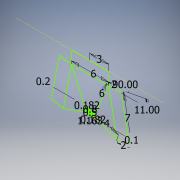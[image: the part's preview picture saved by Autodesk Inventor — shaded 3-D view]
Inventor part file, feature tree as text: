
AUTODESK INVENTOR PART (.ipt)
format: ipt  version: 2019.4 (Build 234330000, 330)  size: 112,128 bytes
history: native  units: in
note: dims shown in document units (in); Inventor stores cm internally (conversion verified against a paired STEP export)
features: sketch x1
ambient origin geometry x8: Origin, YZ Plane, XZ Plane, XY Plane, X Axis, Y Axis, Z Axis, Center Point
feature tree (1):
  sketch  "Sketch1"  dims[d0=0.1181in d18=0.0787in d19=0.0756in d20=0.2756in d21=0.0787in d22=90.0deg d24=0.2362in d32=0.0458in d33=0.0071in d34=0.0071in d35=0.0197in d37=0.0315in d38=0.0079in d39=0.0039in d40=0.2362in d41=0.1575in]
